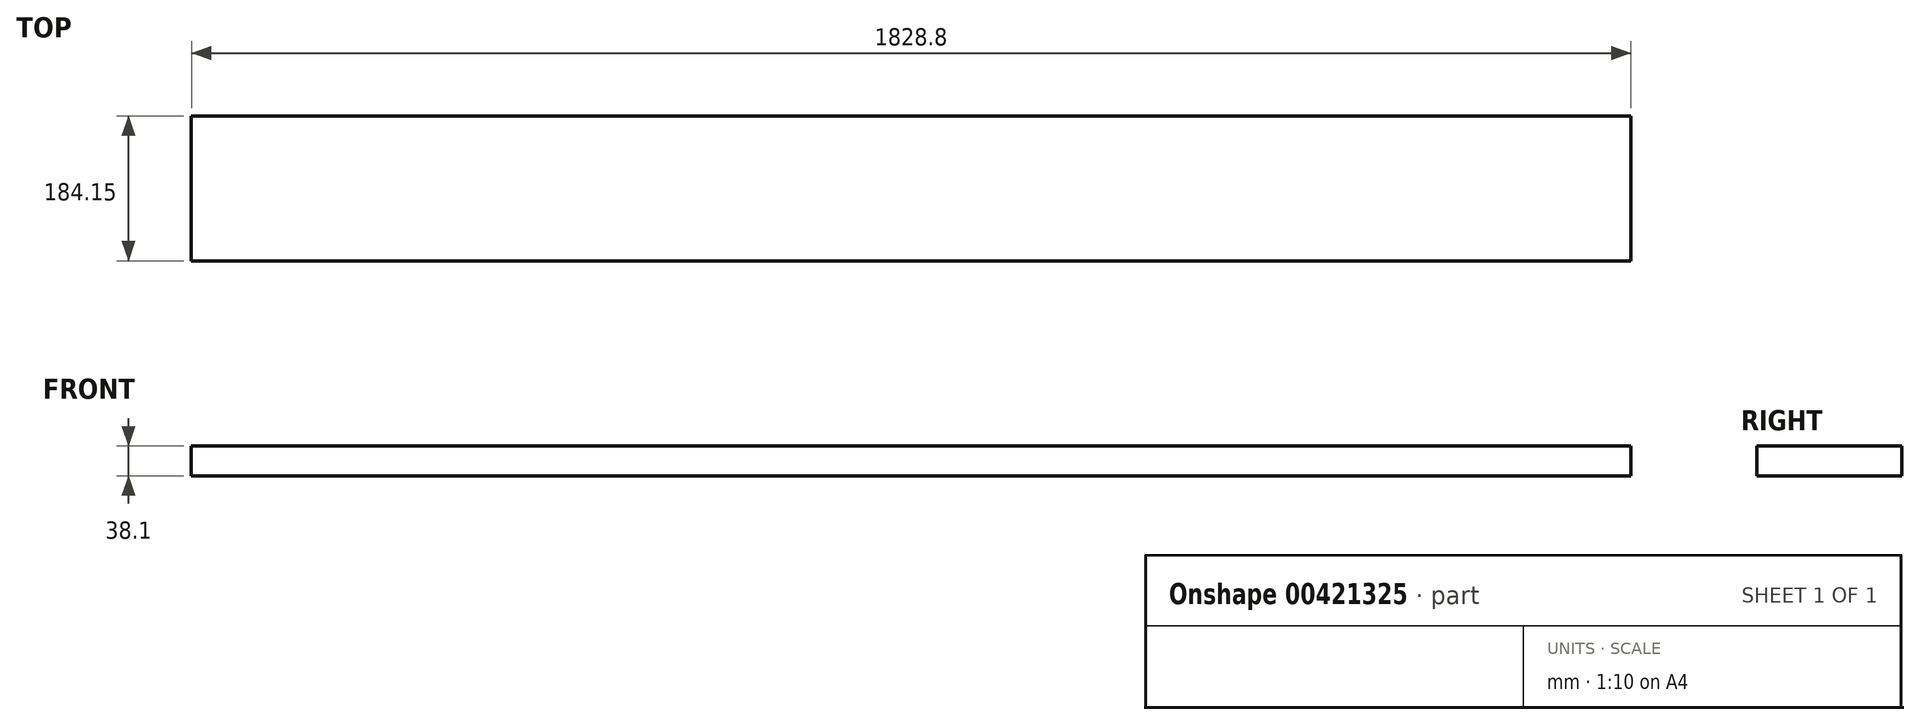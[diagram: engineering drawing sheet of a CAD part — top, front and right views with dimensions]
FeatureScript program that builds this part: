
annotation { "Feature Type Name" : "Feature", "Feature Type Description" : "" }
export const myFeature = defineFeature(function(context is Context, id is Id, definition is map)
    precondition{}
    {
        {
            var Q0;
            Q0=qCreatedBy(makeId("Top.planeOp"),FACE);
            var sketch = newSketch(context, id + "F0", { "sketchPlane" : qUnion([Q0])});
            skLineSegment(sketch, "E0.bottom", {"start": v(-914.15, -246.46) * mm, "end": v(914.65, -246.46) * mm});
            skLineSegment(sketch, "E0.top", {"start": v(-914.15, -62.31) * mm, "end": v(914.65, -62.31) * mm});
            skLineSegment(sketch, "E0.left", {"start": v(-914.15, -246.46) * mm, "end": v(-914.15, -62.31) * mm});
            skLineSegment(sketch, "E0.right", {"start": v(914.65, -246.46) * mm, "end": v(914.65, -62.31) * mm});
            skSolve(sketch);
        }
        {
            var Q0;
            Q0=makeQuery(id+"F0.imprint","IMPRINT",FACE,{"disambiguationData":[TD([[makeQuery(id+"F0.imprint","IMPRINT",EDGE,{"derivedFrom":sQuery(id+"F0.wireOp",EDGE,"E0.bottom")}),1.0]])]});
            extrude(context, id + "F1", {"entities" : qUnion([Q0]), "depth" : 38.1 * mm});
        }
    });
